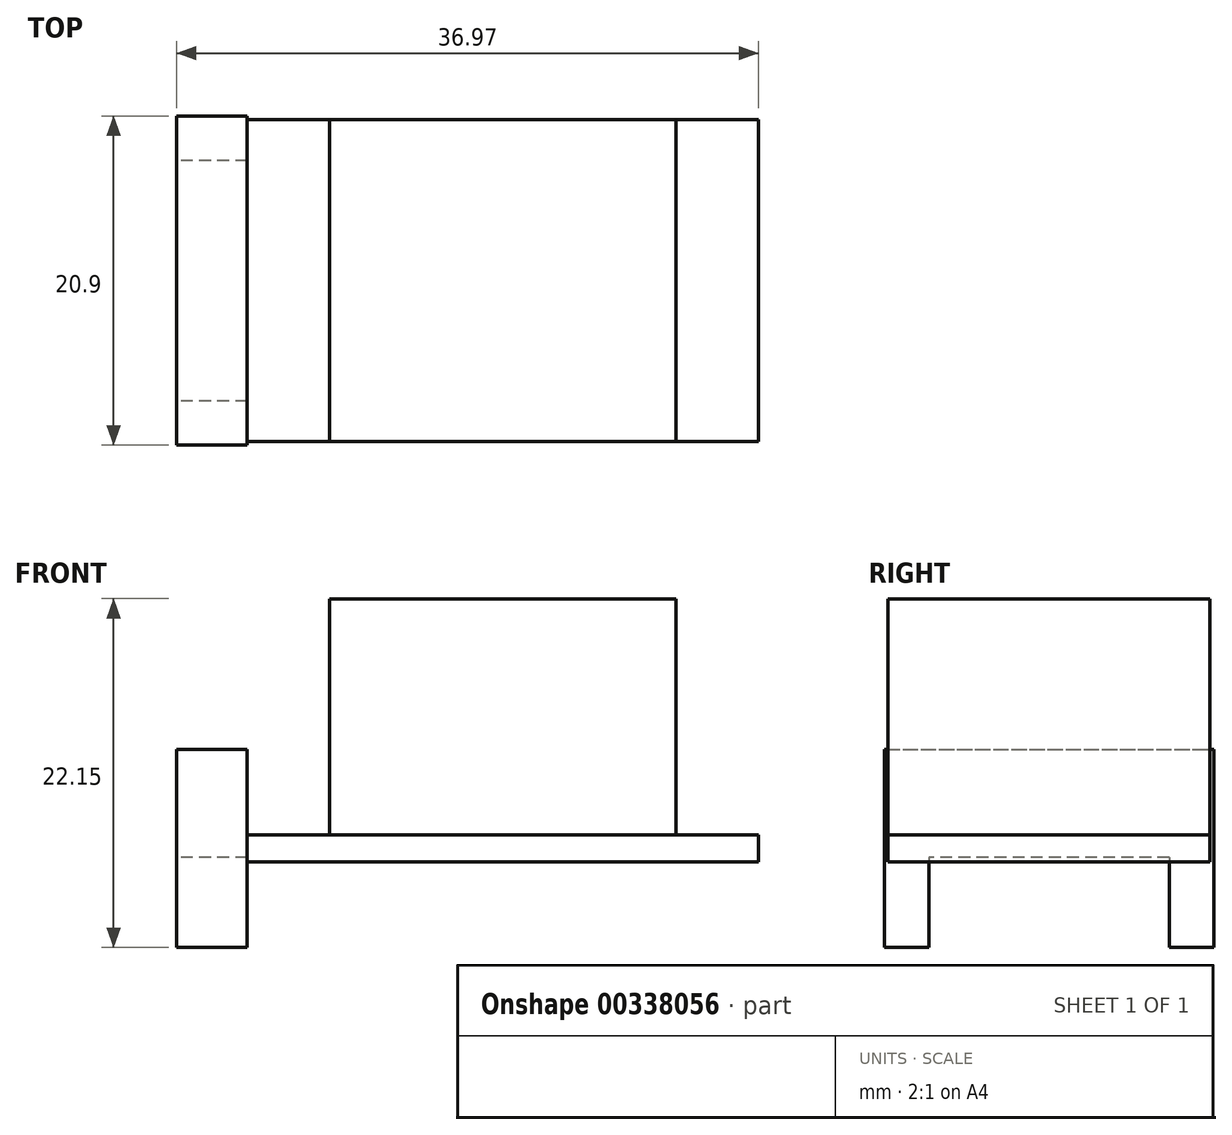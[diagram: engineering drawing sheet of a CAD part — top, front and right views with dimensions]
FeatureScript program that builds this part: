
annotation { "Feature Type Name" : "Feature", "Feature Type Description" : "" }
export const myFeature = defineFeature(function(context is Context, id is Id, definition is map)
    precondition{}
    {
        {
            var Q0;
            Q0=qCreatedBy(makeId("Top.planeOp"),FACE);
            var sketch = newSketch(context, id + "F0", { "sketchPlane" : qUnion([Q0])});
            skLineSegment(sketch, "E0.bottom", {"start": v(16.25, -10.22) * mm, "end": v(-16.25, -10.23) * mm});
            skLineSegment(sketch, "E0.top", {"start": v(16.25, 10.22) * mm, "end": v(-16.25, 10.22) * mm});
            skLineSegment(sketch, "E0.left", {"start": v(16.25, -10.22) * mm, "end": v(16.25, 10.23) * mm});
            skLineSegment(sketch, "E0.right", {"start": v(-16.25, -10.23) * mm, "end": v(-16.25, 10.22) * mm});
            skPoint(sketch, "E0.middle", {"position": v(0, 0) * mm});
            skSolve(sketch);
        }
        {
            var Q0;
            Q0=qSketchRegion(id+"F0",true);
            extrude(context, id + "F1", {"entities" : qUnion([Q0]), "endBound" : BoundingType.SYMMETRIC, "depth" : 1.71 * mm});
        }
        {
            var Q0;
            Q0=makeQuery(id+"F1.opExtrude","SWEPT_FACE",FACE,{"disambiguationData":[OSD([sQuery(id+"F0.wireOp",EDGE,"E0.right")])]});
            var sketch = newSketch(context, id + "F2", { "sketchPlane" : qUnion([Q0])});
            skLineSegment(sketch, "E1.bottom", {"start": v(10.45, -6.29) * mm, "end": v(-10.45, -6.29) * mm});
            skLineSegment(sketch, "E1.top", {"start": v(10.45, 6.29) * mm, "end": v(-10.45, 6.29) * mm});
            skLineSegment(sketch, "E1.left", {"start": v(10.45, -6.28) * mm, "end": v(10.45, 6.29) * mm});
            skLineSegment(sketch, "E1.right", {"start": v(-10.45, -6.29) * mm, "end": v(-10.45, 6.29) * mm});
            skPoint(sketch, "E1.middle", {"position": v(0, 0) * mm});
            skSolve(sketch);
        }
        {
            var Q0;
            Q0=qSketchRegion(id+"F2",true);
            extrude(context, id + "F3", {"entities" : qUnion([Q0]), "depth" : 4.48 * mm});
        }
        {
            var Q0;
            Q0=makeQuery(id+"F3.opExtrude","CAP_FACE",FACE,{"disambiguationData":[OSD([sQuery(id+"F2.wireOp",EDGE,"E1.bottom"),sQuery(id+"F2.wireOp",EDGE,"E1.top"),sQuery(id+"F2.wireOp",EDGE,"E1.left"),sQuery(id+"F2.wireOp",EDGE,"E1.right")])],"isStart":false});
            var sketch = newSketch(context, id + "F4", { "sketchPlane" : qUnion([Q0])});
            skLineSegment(sketch, "E2.bottom", {"start": v(7.64, -6.29) * mm, "end": v(-7.64, -6.29) * mm});
            skLineSegment(sketch, "E2.top", {"start": v(7.64, -0.56) * mm, "end": v(-7.64, -0.57) * mm});
            skLineSegment(sketch, "E2.left", {"start": v(7.64, -6.29) * mm, "end": v(7.64, -0.56) * mm});
            skLineSegment(sketch, "E2.right", {"start": v(-7.64, -6.29) * mm, "end": v(-7.64, -0.57) * mm});
            skPoint(sketch, "E2.middle", {"position": v(0, -3.43) * mm});
            skSolve(sketch);
        }
        {
            var Q0;
            Q0=makeQuery(id+"F4.imprint","IMPRINT",FACE,{"disambiguationData":[TD([[makeQuery(id+"F4.imprint","IMPRINT",EDGE,{"derivedFrom":sQuery(id+"F4.wireOp",EDGE,"E2.bottom")}),-1.0]])]});
            extrude(context, id + "F5", {"entities" : qUnion([Q0]), "operationType" : NewBodyOperationType.REMOVE, "endBound" : BoundingType.UP_TO_NEXT, "oppositeDirection" : true, "depth" : 25 * mm});
        }
        {
            var Q0;
            Q0=makeQuery(id+"F1.opExtrude","CAP_FACE",FACE,{"disambiguationData":[OSD([sQuery(id+"F0.wireOp",EDGE,"E0.bottom"),sQuery(id+"F0.wireOp",EDGE,"E0.top"),sQuery(id+"F0.wireOp",EDGE,"E0.left"),sQuery(id+"F0.wireOp",EDGE,"E0.right")])],"isStart":false});
            var sketch = newSketch(context, id + "F6", { "sketchPlane" : qUnion([Q0])});
            skLineSegment(sketch, "E3.bottom", {"start": v(11, -10.22) * mm, "end": v(-11, -10.22) * mm});
            skLineSegment(sketch, "E3.top", {"start": v(11, 10.22) * mm, "end": v(-11, 10.22) * mm});
            skLineSegment(sketch, "E3.left", {"start": v(11, -10.23) * mm, "end": v(11, 10.23) * mm});
            skLineSegment(sketch, "E3.right", {"start": v(-11, -10.23) * mm, "end": v(-11, 10.23) * mm});
            skPoint(sketch, "E3.middle", {"position": v(0, 0) * mm});
            skSolve(sketch);
        }
        {
            var Q0;
            Q0 = qSketchRegion(id + "F6", true);
            extrude(context, id + "F7", {"entities" : qUnion([Q0]), "depth" : 15 * mm});
        }
    });
